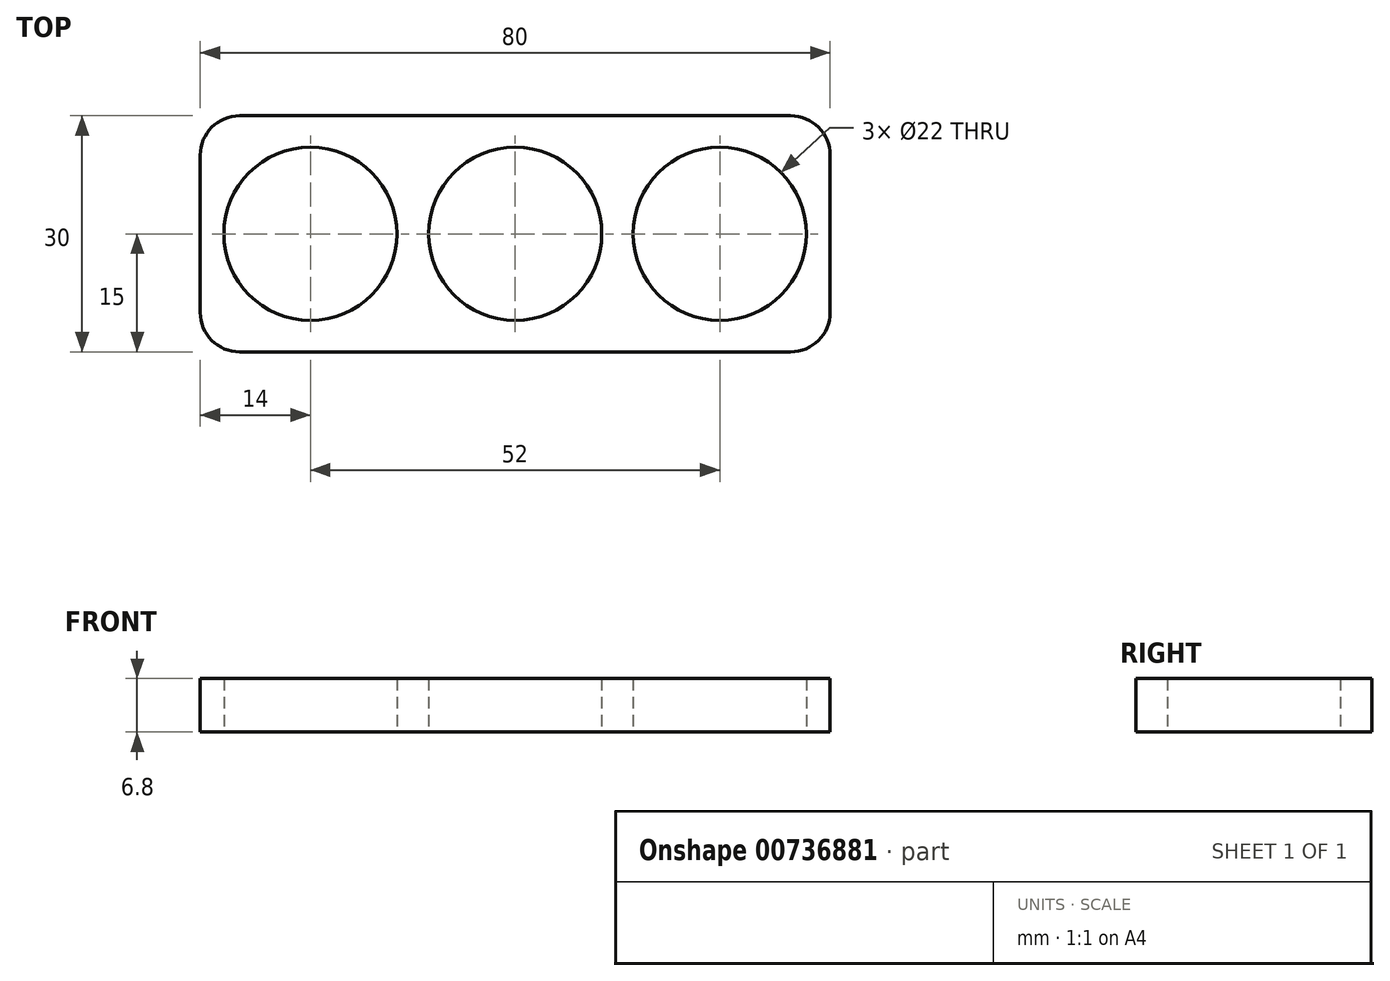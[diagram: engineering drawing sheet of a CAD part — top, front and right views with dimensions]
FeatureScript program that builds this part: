
annotation { "Feature Type Name" : "Feature", "Feature Type Description" : "" }
export const myFeature = defineFeature(function(context is Context, id is Id, definition is map)
    precondition{}
    {
        {
            var Q0;
            Q0=qCreatedBy(makeId("Top.planeOp"),FACE);
            var sketch = newSketch(context, id + "F0", { "sketchPlane" : qUnion([Q0])});
            skLineSegment(sketch, "E0.bottom", {"start": v(-40, 15) * mm, "end": v(40, 15) * mm});
            skLineSegment(sketch, "E0.top", {"start": v(-40, -15) * mm, "end": v(40, -15) * mm});
            skLineSegment(sketch, "E0.left", {"start": v(-40, 15) * mm, "end": v(-40, -15) * mm});
            skLineSegment(sketch, "E0.right", {"start": v(40, 15) * mm, "end": v(40, -15) * mm});
            skPoint(sketch, "E0.middle", {"position": v(0, 0) * mm});
            skCircle(sketch, "E1", {"center": v(0, 0) * mm, "radius": 11 * mm});
            skCircle(sketch, "E2", {"center": v(-26, 0) * mm, "radius": 11 * mm});
            skPoint(sketch, "E2.centerSnap0", {"position": v(-40, 0) * mm});
            skCircle(sketch, "E3", {"center": v(26, 0) * mm, "radius": 11 * mm});
            skLineSegment(sketch, "E4", {"start": v(-26, 0) * mm, "end": v(0, 0) * mm});
            skLineSegment(sketch, "E5", {"start": v(0, 0) * mm, "end": v(26, 0) * mm});
            skSolve(sketch);
        }
        {
            var Q0;
            Q0=makeQuery(id+"F0.imprint","IMPRINT",FACE,{"disambiguationData":[TD([[makeQuery(id+"F0.imprint","IMPRINT",EDGE,{"derivedFrom":sQuery(id+"F0.wireOp",EDGE,"E2")}),1.0]])]});
            var Q1;
            Q1=makeQuery(id+"F0.imprint","IMPRINT",FACE,{"disambiguationData":[TD([[makeQuery(id+"F0.imprint","IMPRINT",EDGE,{"derivedFrom":sQuery(id+"F0.wireOp",EDGE,"E3")}),1.0]])]});
            var Q2;
            {var subQ0=sQuery(id+"F0.wireOp",EDGE,"E4");var subQ1=sQuery(id+"F0.wireOp",EDGE,"E1");var subQ2=makeQuery(id+"F0.imprint","INTERSECT",VERTEX,{"derivedFrom":[subQ1,subQ0]});Q2=makeQuery(id+"F0.imprint","IMPRINT",FACE,{"disambiguationData":[TD([[makeQuery(id+"F0.imprint","IMPRINT",EDGE,{"disambiguationData":[TD([[subQ2,1.0]])],"derivedFrom":subQ1}),1.0]])]});}
            var Q3;
            {var subQ0=sQuery(id+"F0.wireOp",EDGE,"E4");var subQ1=sQuery(id+"F0.wireOp",EDGE,"E1");var subQ2=makeQuery(id+"F0.imprint","INTERSECT",VERTEX,{"derivedFrom":[subQ1,subQ0]});Q3=makeQuery(id+"F0.imprint","IMPRINT",FACE,{"disambiguationData":[TD([[makeQuery(id+"F0.imprint","IMPRINT",EDGE,{"disambiguationData":[TD([[subQ2,-1.0]])],"derivedFrom":subQ1}),1.0]])]});}
            var Q4;
            Q4=makeQuery(id+"F0.imprint","IMPRINT",FACE,{"disambiguationData":[TD([[makeQuery(id+"F0.imprint","IMPRINT",EDGE,{"derivedFrom":sQuery(id+"F0.wireOp",EDGE,"E0.bottom")}),-1.0]])]});
            extrude(context, id + "F1", {"entities" : qUnion([Q0, Q1, Q2, Q3, Q4]), "depth" : 6.8 * mm, "offsetDistance" : 25 * mm});
        }
        {
            var Q0;
            Q0=makeQuery(id+"F1.opExtrude","CAP_FACE",FACE,{"disambiguationData":[OSD([sQuery(id+"F0.wireOp",EDGE,"E0.bottom"),sQuery(id+"F0.wireOp",EDGE,"E0.top"),sQuery(id+"F0.wireOp",EDGE,"E0.left"),sQuery(id+"F0.wireOp",EDGE,"E0.right")])],"isStart":true});
            var sketch = newSketch(context, id + "F2", { "sketchPlane" : qUnion([Q0])});
            skCircle(sketch, "E6", {"center": v(0, 0) * mm, "radius": 11 * mm});
            skCircle(sketch, "E7", {"center": v(26, 0) * mm, "radius": 11 * mm});
            skCircle(sketch, "E8", {"center": v(-26, 0) * mm, "radius": 11 * mm});
            skSolve(sketch);
        }
        {
            var Q0;
            Q0=makeQuery(id+"F2.imprint","IMPRINT",FACE,{"disambiguationData":[TD([[makeQuery(id+"F2.imprint","IMPRINT",EDGE,{"derivedFrom":sQuery(id+"F2.wireOp",EDGE,"E7")}),1.0]])]});
            var Q1;
            Q1=makeQuery(id+"F2.imprint","IMPRINT",FACE,{"disambiguationData":[TD([[makeQuery(id+"F2.imprint","IMPRINT",EDGE,{"derivedFrom":sQuery(id+"F2.wireOp",EDGE,"E6")}),1.0]])]});
            var Q2;
            Q2=makeQuery(id+"F2.imprint","IMPRINT",FACE,{"disambiguationData":[TD([[makeQuery(id+"F2.imprint","IMPRINT",EDGE,{"derivedFrom":sQuery(id+"F2.wireOp",EDGE,"E8")}),1.0]])]});
            extrude(context, id + "F3", {"entities" : qUnion([Q0, Q1, Q2]), "operationType" : NewBodyOperationType.REMOVE, "oppositeDirection" : true, "depth" : 25 * mm, "offsetDistance" : 25 * mm});
        }
        {
            var Q0;
            Q0=makeQuery(id+"F1.opExtrude","SWEPT_EDGE",EDGE,{"disambiguationData":[OSD([sQuery(id+"F0.wireOp",EDGE,"E0.top"),sQuery(id+"F0.wireOp",EDGE,"E0.left")])]});
            var Q1;
            Q1=makeQuery(id+"F1.opExtrude","SWEPT_EDGE",EDGE,{"disambiguationData":[OSD([sQuery(id+"F0.wireOp",EDGE,"E0.bottom"),sQuery(id+"F0.wireOp",EDGE,"E0.left")])]});
            var Q2;
            Q2=makeQuery(id+"F1.opExtrude","SWEPT_EDGE",EDGE,{"disambiguationData":[OSD([sQuery(id+"F0.wireOp",EDGE,"E0.bottom"),sQuery(id+"F0.wireOp",EDGE,"E0.right")])]});
            var Q3;
            Q3=makeQuery(id+"F1.opExtrude","SWEPT_EDGE",EDGE,{"disambiguationData":[OSD([sQuery(id+"F0.wireOp",EDGE,"E0.top"),sQuery(id+"F0.wireOp",EDGE,"E0.right")])]});
            fillet(context, id + "F4", {"entities" : qUnion([Q0, Q1, Q2, Q3]), "radius" : 5 * mm, "tangentPropagation" : true, "allowEdgeOverflow" : false});
        }
    });
